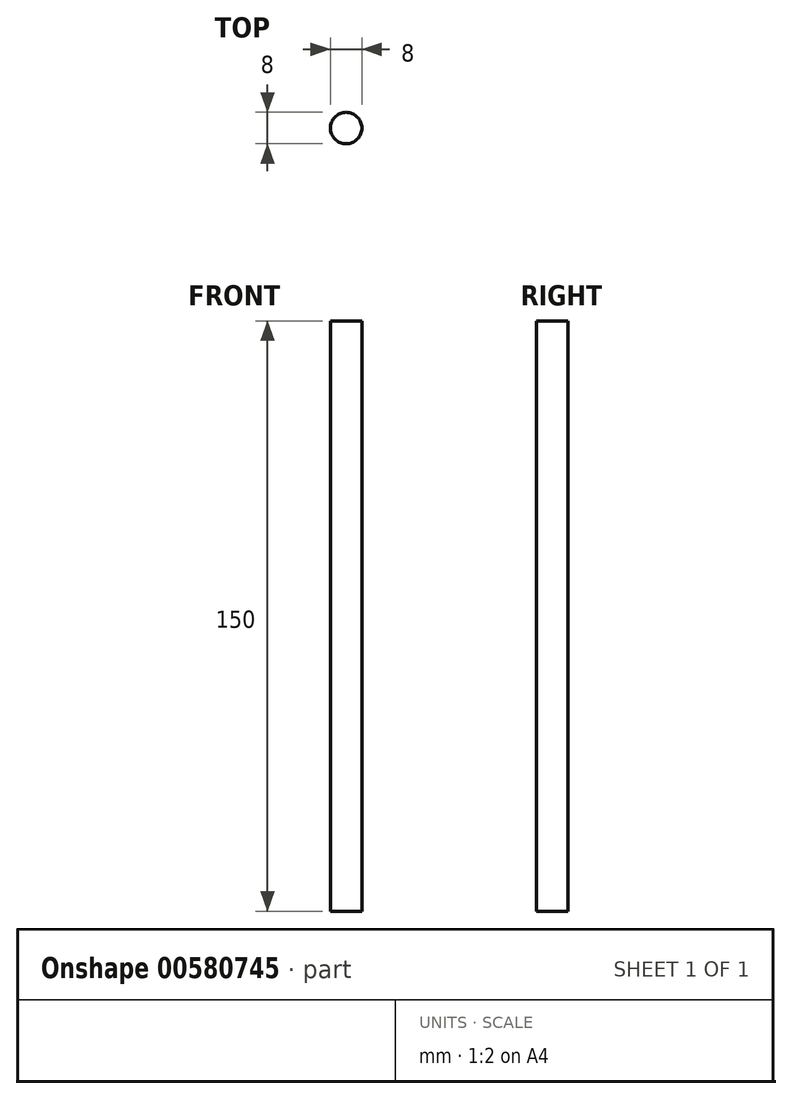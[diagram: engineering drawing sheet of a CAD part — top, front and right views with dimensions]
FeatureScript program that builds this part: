
annotation { "Feature Type Name" : "Feature", "Feature Type Description" : "" }
export const myFeature = defineFeature(function(context is Context, id is Id, definition is map)
    precondition{}
    {
        {
            var Q0;
            Q0=qCreatedBy(makeId("Top.planeOp"),FACE);
            var sketch = newSketch(context, id + "F0", { "sketchPlane" : qUnion([Q0])});
            skCircle(sketch, "E0", {"center": v(0, -1.2) * mm, "radius": 4 * mm});
            skSolve(sketch);
        }
        {
            var Q0;
            Q0=makeQuery(id+"F0.imprint","IMPRINT",FACE,{"disambiguationData":[TD([[makeQuery(id+"F0.imprint","IMPRINT",EDGE,{"derivedFrom":sQuery(id+"F0.wireOp",EDGE,"E0")}),1.0]])]});
            extrude(context, id + "F1", {"entities" : qUnion([Q0]), "depth" : 150 * mm, "offsetDistance" : 25.4 * mm});
        }
    });
